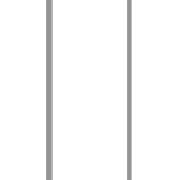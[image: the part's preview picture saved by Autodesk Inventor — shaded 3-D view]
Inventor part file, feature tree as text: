
AUTODESK INVENTOR PART (.ipt)
format: ipt  version: 2021 (Build 250183000, 183)  size: 142,848 bytes
history: native  units: in
note: dims shown in document units (in); Inventor stores cm internally (conversion verified against a paired STEP export)
features: other x4, sketch x4, plane x2, hole x1
ambient origin geometry x8: Origin, YZ Plane, XZ Plane, XY Plane, X Axis, Y Axis, Z Axis, Center Point
bodies: Solid1 (feature_tree), Body (feature_tree)
feature tree (11):
  other  "Driven Length"
  other  "Frame Generator"
  plane  "Work Plane3"
  other  "Start Plane"
  other  "End Plane"
  hole  "Hole2"  [1 undecoded]
  sketch  "Sketch"  dims[d4=2.0in d16=-0.0in d17=2.0in d18=0.12in d19=0.0in d22=1.5in d23=0.4375in d24=0.75in d25=0.635in d26=0.25in d27=0.5635in d28=1.0in d29=0.8108in d32=90.0deg d21=2.0in d8=0.5in d9=0.0344in d10=0.5in d11=0.0344in]
  sketch  "Sketch5"  dims[d0=1.5in d1=1.0in]
  sketch  "Sketch8"  dims[d2=0.0625in]
  plane  "Work Plane6"
  sketch  "Sketch9"  dims[d3=0.0625in]
note: 1 required parameter value undecoded (feature->parameter linkage not recoverable at this tier; creation-order binding heuristic only, values carry confidence <= 0.55)
